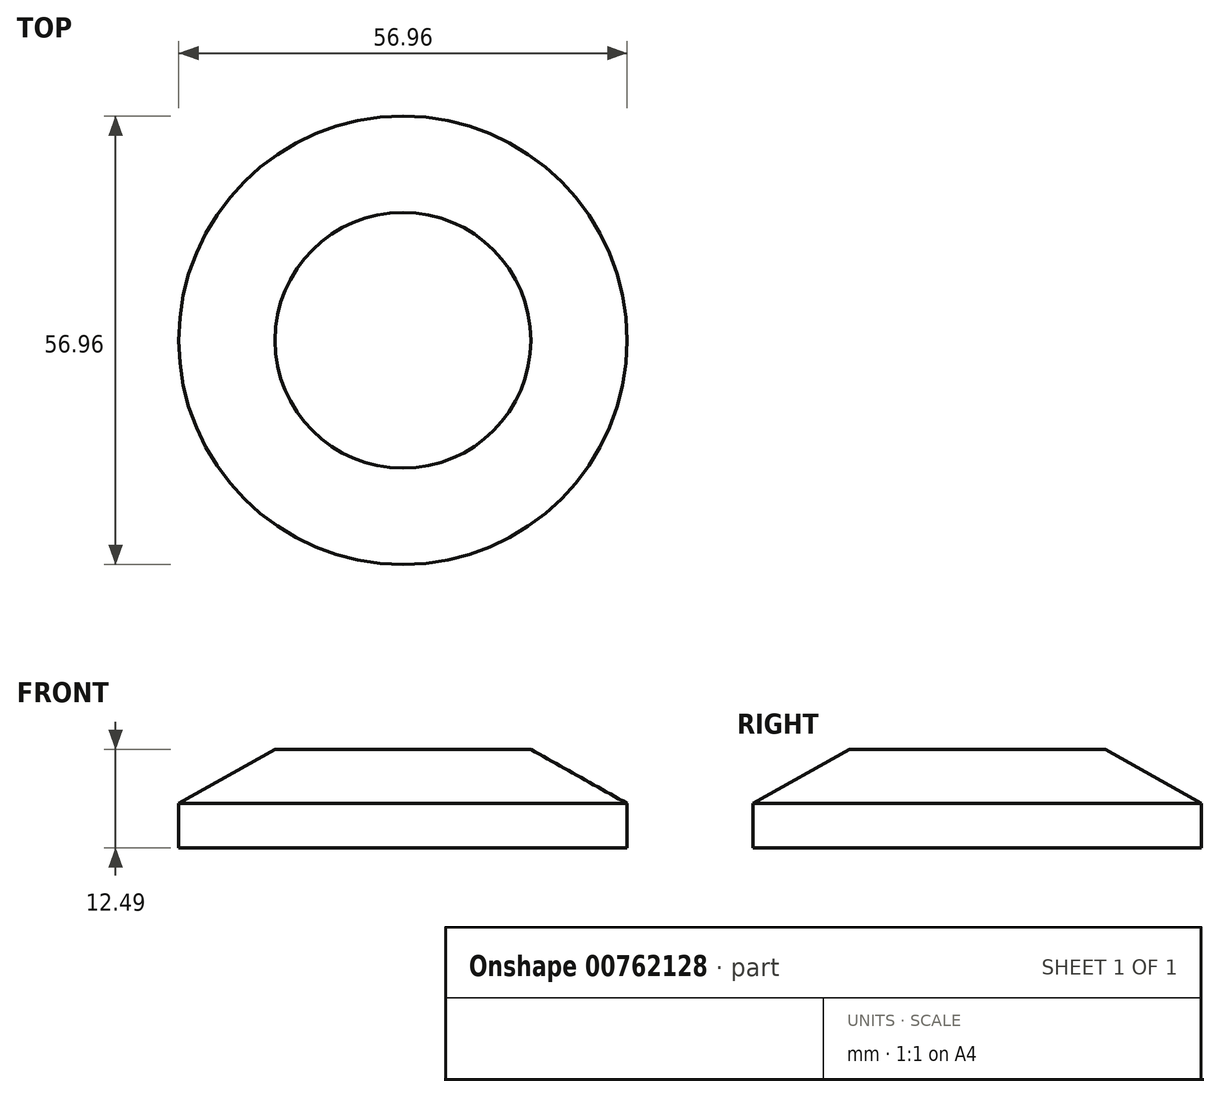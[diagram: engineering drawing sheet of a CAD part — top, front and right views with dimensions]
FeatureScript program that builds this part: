
annotation { "Feature Type Name" : "Feature", "Feature Type Description" : "" }
export const myFeature = defineFeature(function(context is Context, id is Id, definition is map)
    precondition{}
    {
        {
            var Q0;
            Q0=qCreatedBy(makeId("Front.planeOp"),FACE);
            var sketch = newSketch(context, id + "F0", { "sketchPlane" : qUnion([Q0])});
            skLineSegment(sketch, "E0", {"start": v(0, 0) * mm, "end": v(28.48, 0) * mm});
            skLineSegment(sketch, "E1", {"start": v(28.48, 0) * mm, "end": v(28.48, 5.63) * mm});
            skLineSegment(sketch, "E2", {"start": v(28.48, 5.63) * mm, "end": v(16.25, 12.5) * mm});
            skLineSegment(sketch, "E3", {"start": v(16.25, 12.5) * mm, "end": v(0, 12.5) * mm});
            skLineSegment(sketch, "E4", {"start": v(0, 12.5) * mm, "end": v(0, 0) * mm});
            skSolve(sketch);
        }
        {
            var Q0;
            Q0=makeQuery(id+"F0.imprint","IMPRINT",FACE,{"disambiguationData":[TD([[makeQuery(id+"F0.imprint","IMPRINT",EDGE,{"derivedFrom":sQuery(id+"F0.wireOp",EDGE,"E0")}),1.0]])]});
            var Q1;
            Q1=sQuery(id+"F0.wireOp",EDGE,"E4");
            revolve(context, id + "F1", {"surfaceOperationType" : NewSurfaceOperationType.NEW, "entities" : qUnion([Q0]), "axis" : qUnion([Q1]), "revolveType" : RevolveType.FULL});
        }
    });
